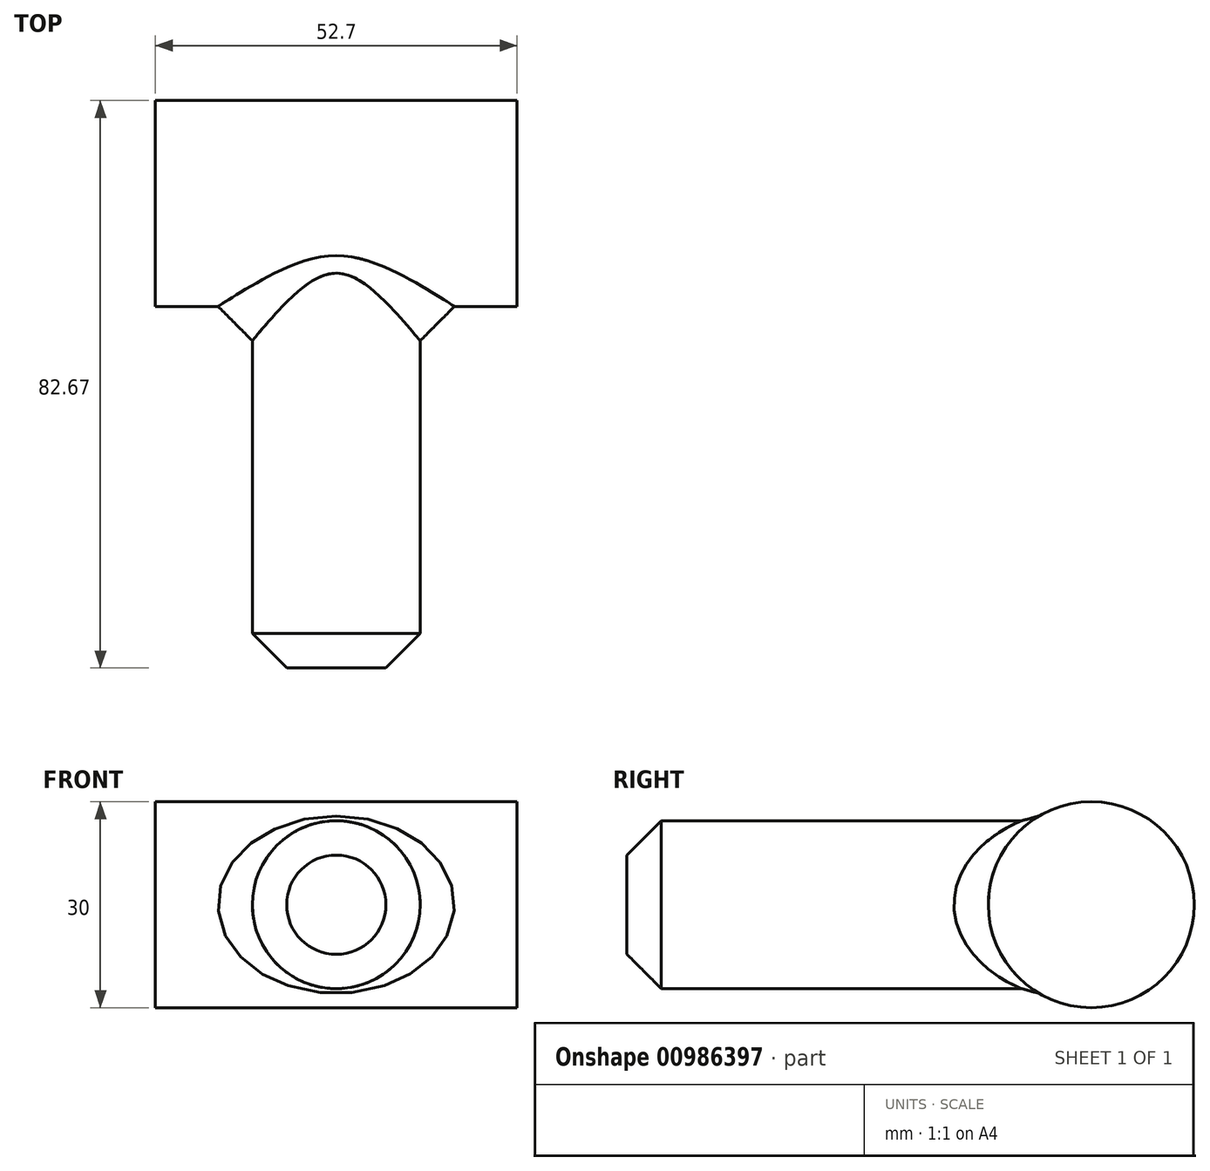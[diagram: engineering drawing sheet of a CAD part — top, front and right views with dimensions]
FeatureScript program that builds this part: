
annotation { "Feature Type Name" : "Feature", "Feature Type Description" : "" }
export const myFeature = defineFeature(function(context is Context, id is Id, definition is map)
    precondition{}
    {
        {
            var Q0;
            Q0=qCreatedBy(makeId("Right.planeOp"),FACE);
            var sketch = newSketch(context, id + "F0", { "sketchPlane" : qUnion([Q0])});
            skCircle(sketch, "E0", {"center": v(0, 0) * mm, "radius": 15 * mm});
            skSolve(sketch);
        }
        {
            var Q0;
            Q0=makeQuery(id+"F0.imprint","IMPRINT",FACE,{"disambiguationData":[TD([[makeQuery(id+"F0.imprint","IMPRINT",EDGE,{"derivedFrom":sQuery(id+"F0.wireOp",EDGE,"E0")}),1.0]])]});
            var Q1;
            Q1=sQuery(id+"F0.wireOp",EDGE,"E0");
            extrude(context, id + "F1", {"entities" : qUnion([Q0]), "surfaceEntities" : qUnion([Q1]), "endBound" : BoundingType.SYMMETRIC, "depth" : 52.7 * mm, "offsetDistance" : 25 * mm});
        }
        {
            var Q0;
            Q0=qCreatedBy(makeId("Front.planeOp"),FACE);
            var sketch = newSketch(context, id + "F2", { "sketchPlane" : qUnion([Q0])});
            skCircle(sketch, "E1", {"center": v(0, 0) * mm, "radius": 12.23 * mm});
            skSolve(sketch);
        }
        {
            var Q0;
            Q0=qSketchRegion(id+"F2",true);
            var Q1;
            Q1=makeQuery(id+"F1.opExtrude","SWEPT_FACE",FACE,{"disambiguationData":[OSD([sQuery(id+"F0.wireOp",EDGE,"E0")])]});
            extrude(context, id + "F3", {"entities" : qUnion([Q0]), "operationType" : NewBodyOperationType.ADD, "endBound" : BoundingType.THROUGH_ALL, "depth" : 25 * mm, "endBoundEntityFace" : qUnion([Q1]), "hasOffset" : true, "offsetDistance" : 3 * mm, "offsetOppositeDirection" : true});
        }
        {
            var Q0;
            Q0=makeQuery(id+"F3.opExtrude","CAP_EDGE",EDGE,{"disambiguationData":[OSD([sQuery(id+"F2.wireOp",EDGE,"E1")])],"isStart":false});
            var Q1;
            Q1=makeQuery(id+"F3.boolean.opBoolean","INTERSECT",EDGE,{"derivedFrom":[makeQuery(id+"F1.opExtrude","SWEPT_FACE",FACE,{"disambiguationData":[OSD([sQuery(id+"F0.wireOp",EDGE,"E0")])]}),makeQuery(id+"F3.opExtrude","SWEPT_FACE",FACE,{"disambiguationData":[OSD([sQuery(id+"F2.wireOp",EDGE,"E1")])]})]});
            chamfer(context, id + "F4", {"entities" : qUnion([Q0, Q1]), "width" : 5 * mm, "tangentPropagation" : true});
        }
    });
